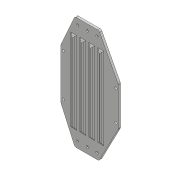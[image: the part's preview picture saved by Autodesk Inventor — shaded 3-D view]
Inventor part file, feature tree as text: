
AUTODESK INVENTOR PART (.ipt)
format: ipt  version: 2018 (Build 220112000, 112)  size: 618,496 bytes
history: native  units: mm
features: sketch x17, extrude x13, projected_geometry x12, fillet x6, hole x5, chamfer x3, plane x1, mirror x1, pattern_linear x1
ambient origin geometry x8: Origin, YZ Plane, XZ Plane, XY Plane, X Axis, Y Axis, Z Axis, Center Point
bodies: Solid1 (feature_tree)
feature tree (59):
  extrude  "Extrusion1"  Depth=76.0mm
  hole  "Hole1"  [1 undecoded]
  extrude  "Extrusion2"  Depth=40.0mm
  extrude  "Extrusion5"  Depth=2.0mm
  extrude  "Extrusion3"  Depth=3.0mm TaperAngle=0.0deg
  extrude  "Extrusion4"  Depth=3.0mm TaperAngle=0.0deg
  sketch  "Sketch8"  dims[d18=43.0mm d20=3.0mm d21=0.0mm]
  hole  "Hole2"  [1 undecoded]
  hole  "Hole3"  [1 undecoded]
  extrude  "Extrusion6"  Depth=17.0624mm
  extrude  "Extrusion7"  Depth=2.0mm
  extrude  "Extrusion10"  Depth=3.0mm TaperAngle=0.0deg
  chamfer  "Chamfer3"  Distance=4.957359mm
  plane  "Work Plane1"
  extrude  "Extrusion11"  Depth=2.0mm TaperAngle=0.0deg
  fillet  "Fillet1"  Radius=4.957359mm
  extrude  "Extrusion12"  TaperAngle=0.0deg  [1 undecoded]
  chamfer  "Chamfer4"  Distance=11.2mm
  chamfer  "Chamfer5"  Distance=10.0mm Angle=45.0deg
  fillet  "Fillet2"  [1 undecoded]
  fillet  "Fillet3"  Radius=8.0mm
  extrude  "Extrusion13"  Depth=2.0mm
  fillet  "Fillet4"  Radius=9.5mm
  hole  "Hole4"  [1 undecoded]
  mirror  "Mirror2"
  extrude  "Extrusion14"  Depth=2.0mm TaperAngle=0.0deg
  hole  "Hole5"  [1 undecoded]
  fillet  "Fillet5"  Radius=18.0mm
  extrude  "Extrusion15"  Depth=2.0mm TaperAngle=0.0deg
  fillet  "Fillet6"  Radius=10.0mm
  pattern_linear  "Rectangular Pattern1"  Spacing1=4.24mm  [1 undecoded]
  sketch  "Sketch1"  dims[d0=76.0mm d1=143.6mm]
  sketch  "Sketch2"  dims[d2=3.0mm d3=0.0mm d4=8.0mm]
  sketch  "Sketch4"  dims[d5=70.0mm d6=40.0mm]
  sketch  "Sketch5"  dims[d7=3.2mm d8=6.0mm d9=6.3mm d10=2.0mm d11=90.0deg d12=8.0mm d13=20.594885mm d14=38.0mm]
  projected_geometry  "Projected Loop1"
  sketch  "Sketch7"  dims[d15=17.0mm d16=3.0mm d17=0.0mm]
  projected_geometry  "Projected Loop3"
  projected_geometry  "Projected Loop4"
  sketch  "Sketch10"  dims[d22=25.4mm d23=3.0mm d24=0.0mm]
  projected_geometry  "Projected Loop5"
  sketch  "Sketch11"  dims[d25=14.0mm d26=12.7mm]
  projected_geometry  "Projected Loop6"
  sketch  "Sketch12"  dims[d27=17.4625mm d30=17.0624mm]
  projected_geometry  "Projected Loop7"
  sketch  "Sketch16"  dims[d31=5.0mm]
  projected_geometry  "Projected Loop11"
  projected_geometry  "Projected Loop12"
  sketch  "Sketch17"  dims[d32=4.3mm d33=6.0mm d34=9.4mm d35=2.0mm d36=90.0deg d37=8.0mm d38=20.594885mm]
  projected_geometry  "Projected Loop13"
  sketch  "Sketch18"  dims[d39=5.3mm d40=6.0mm d41=10.4mm d42=2.0mm d43=90.0deg d44=8.0mm d45=20.594885mm d46=46.0mm]
  projected_geometry  "Projected Loop14"
  sketch  "Sketch19"  dims[d47=24.0mm d48=3.0mm d49=0.0mm]
  sketch  "Sketch20"  dims[d50=135.0deg]
  sketch  "Sketch21"  dims[d51=135.0deg]
  sketch  "Sketch22"  dims[d52=7.0mm]
  projected_geometry  "Projected Loop15"
  sketch  "Sketch23"  dims[d53=6.0mm d54=4.957359mm d55=50.0mm d56=0.0mm d57=4.957359mm d58=0.0mm d59=0.0mm d71=11.2mm d72=0.0mm d73=11.2mm d74=10.0mm d75=45.0deg d76=-18.0mm d77=8.0mm d78=8.0mm d79=9.5mm d80=9.5mm d81=15.0mm d82=0.0mm d83=2.0mm d84=18.0mm d85=15.0mm d86=0.0mm d87=15.0mm d88=10.0mm d89=45.0deg d90=4.24mm d91=10.0mm d92=45.0deg d93=1.0mm d94=3.0mm d95=15.0mm d96=0.0mm d97=1.0mm d98=26.0mm d99=10.0mm d100=12.0mm d101=2.459mm d102=6.0mm d103=10.4mm d104=2.0mm d105=90.0deg d106=10.0mm d107=20.594885mm d108=15.0mm d109=0.0mm d110=3.2mm d111=6.0mm d112=6.3mm d113=2.0mm d114=90.0deg d115=10.0mm d116=20.594885mm d117=3.0mm d118=4.0mm d119=105.0mm d120=15.0mm d121=2.0mm d122=0.0mm d123=2.0mm d124=40.0mm d126=12.0mm]
  projected_geometry  "Projected Loop16"
note: 8 required parameter values undecoded (feature->parameter linkage not recoverable at this tier; creation-order binding heuristic only, values carry confidence <= 0.55)
